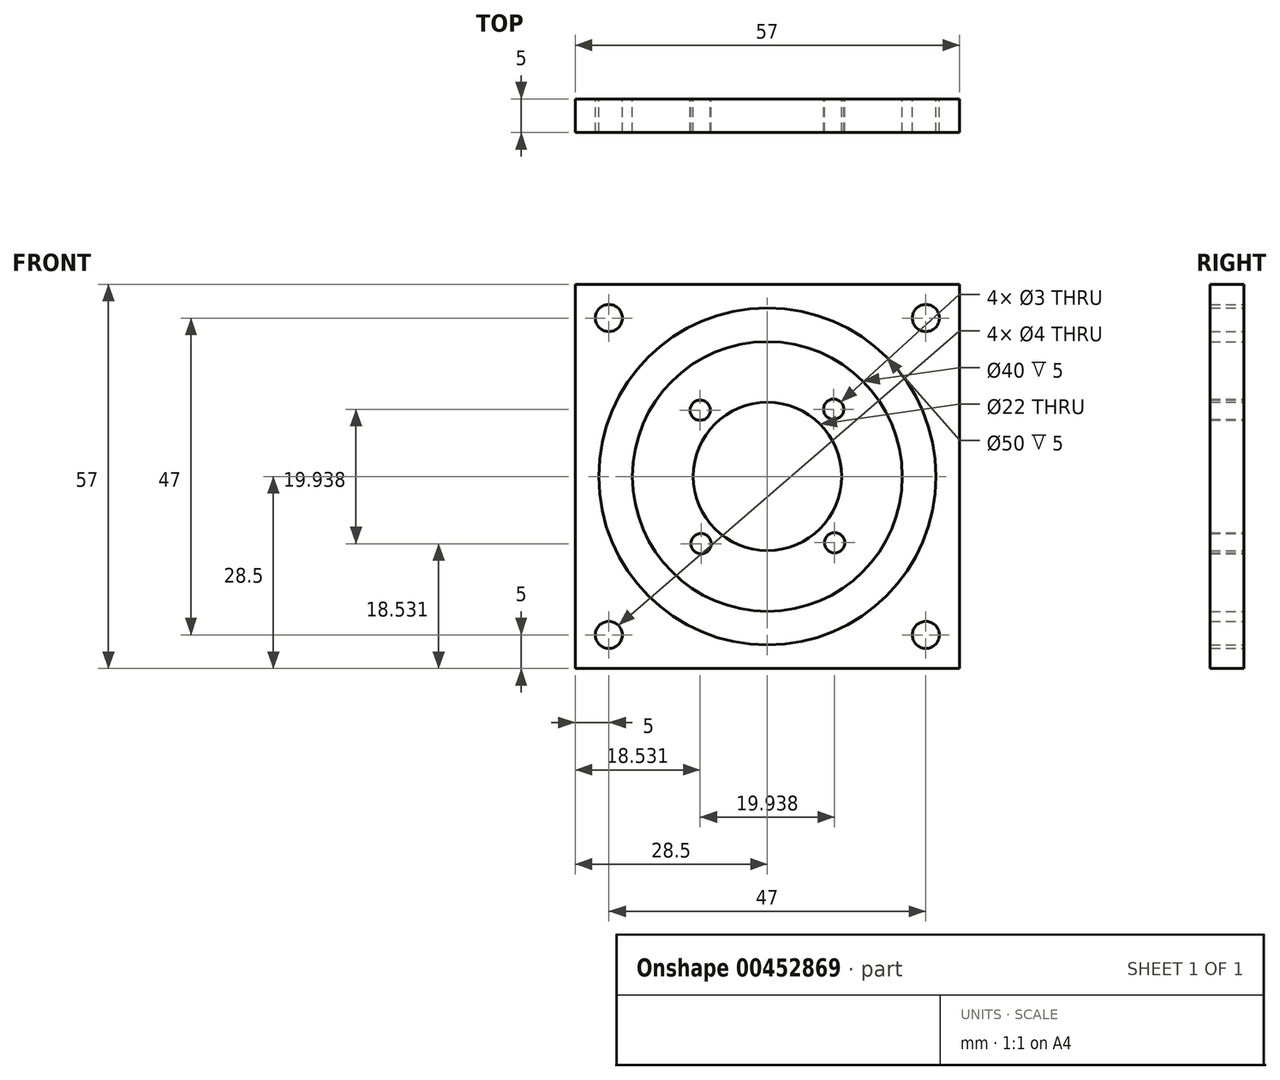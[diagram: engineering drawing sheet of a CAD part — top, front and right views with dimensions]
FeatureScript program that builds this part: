
annotation { "Feature Type Name" : "Feature", "Feature Type Description" : "" }
export const myFeature = defineFeature(function(context is Context, id is Id, definition is map)
    precondition{}
    {
        {
            var Q0;
            Q0=qCreatedBy(makeId("Front.planeOp"),FACE);
            var sketch = newSketch(context, id + "F0", { "sketchPlane" : qUnion([Q0])});
            skLineSegment(sketch, "E0.bottom", {"start": v(-28.5, -28.5) * mm, "end": v(28.5, -28.5) * mm});
            skLineSegment(sketch, "E0.top", {"start": v(-28.5, 28.5) * mm, "end": v(28.5, 28.5) * mm});
            skLineSegment(sketch, "E0.left", {"start": v(-28.5, -28.5) * mm, "end": v(-28.5, 28.5) * mm});
            skLineSegment(sketch, "E0.right", {"start": v(28.5, -28.5) * mm, "end": v(28.5, 28.5) * mm});
            skPoint(sketch, "E0.middle", {"position": v(0, 0) * mm});
            skCircle(sketch, "E1", {"center": v(-23.5, 23.5) * mm, "radius": 2 * mm});
            skCircle(sketch, "E2", {"center": v(23.5, 23.5) * mm, "radius": 2 * mm});
            skCircle(sketch, "E3", {"center": v(23.5, -23.5) * mm, "radius": 2 * mm});
            skCircle(sketch, "E4", {"center": v(-23.5, -23.5) * mm, "radius": 2 * mm});
            skCircle(sketch, "E5", {"center": v(0, 0) * mm, "radius": 25 * mm});
            skCircle(sketch, "E6", {"center": v(0, 0) * mm, "radius": 20 * mm});
            skCircle(sketch, "E7", {"center": v(-9.97, 9.83) * mm, "radius": 1.5 * mm});
            skCircle(sketch, "E8.1.0", {"center": v(-9.83, -9.97) * mm, "radius": 1.5 * mm});
            skCircle(sketch, "E8.2.0", {"center": v(9.97, -9.83) * mm, "radius": 1.5 * mm});
            skCircle(sketch, "E8.3.0", {"center": v(9.83, 9.97) * mm, "radius": 1.5 * mm});
            skCircle(sketch, "E9", {"center": v(0, 0) * mm, "radius": 11 * mm});
            skSolve(sketch);
        }
        {
            var Q0;
            Q0=makeQuery(id+"F0.imprint","IMPRINT",FACE,{"disambiguationData":[TD([[makeQuery(id+"F0.imprint","IMPRINT",EDGE,{"derivedFrom":sQuery(id+"F0.wireOp",EDGE,"E0.bottom")}),1.0]])]});
            extrude(context, id + "F1", {"entities" : qUnion([Q0]), "depth" : 5 * mm});
        }
        {
            var Q0;
            Q0=makeQuery(id+"F0.imprint","IMPRINT",FACE,{"disambiguationData":[TD([[makeQuery(id+"F0.imprint","IMPRINT",EDGE,{"derivedFrom":sQuery(id+"F0.wireOp",EDGE,"E5")}),1.0]])]});
            extrude(context, id + "F2", {"entities" : qUnion([Q0]), "depth" : 5 * mm});
        }
        {
            var Q0;
            Q0=makeQuery(id+"F0.imprint","IMPRINT",FACE,{"disambiguationData":[TD([[makeQuery(id+"F0.imprint","IMPRINT",EDGE,{"derivedFrom":sQuery(id+"F0.wireOp",EDGE,"E6")}),1.0]])]});
            var Q1;
            Q1=makeQuery(id+"F0.imprint","IMPRINT",FACE,{"disambiguationData":[TD([[makeQuery(id+"F0.imprint","IMPRINT",EDGE,{"derivedFrom":sQuery(id+"F0.wireOp",EDGE,"E5")}),1.0]])]});
            extrude(context, id + "F3", {"entities" : qUnion([Q0, Q1]), "depth" : 5 * mm});
        }
    });
